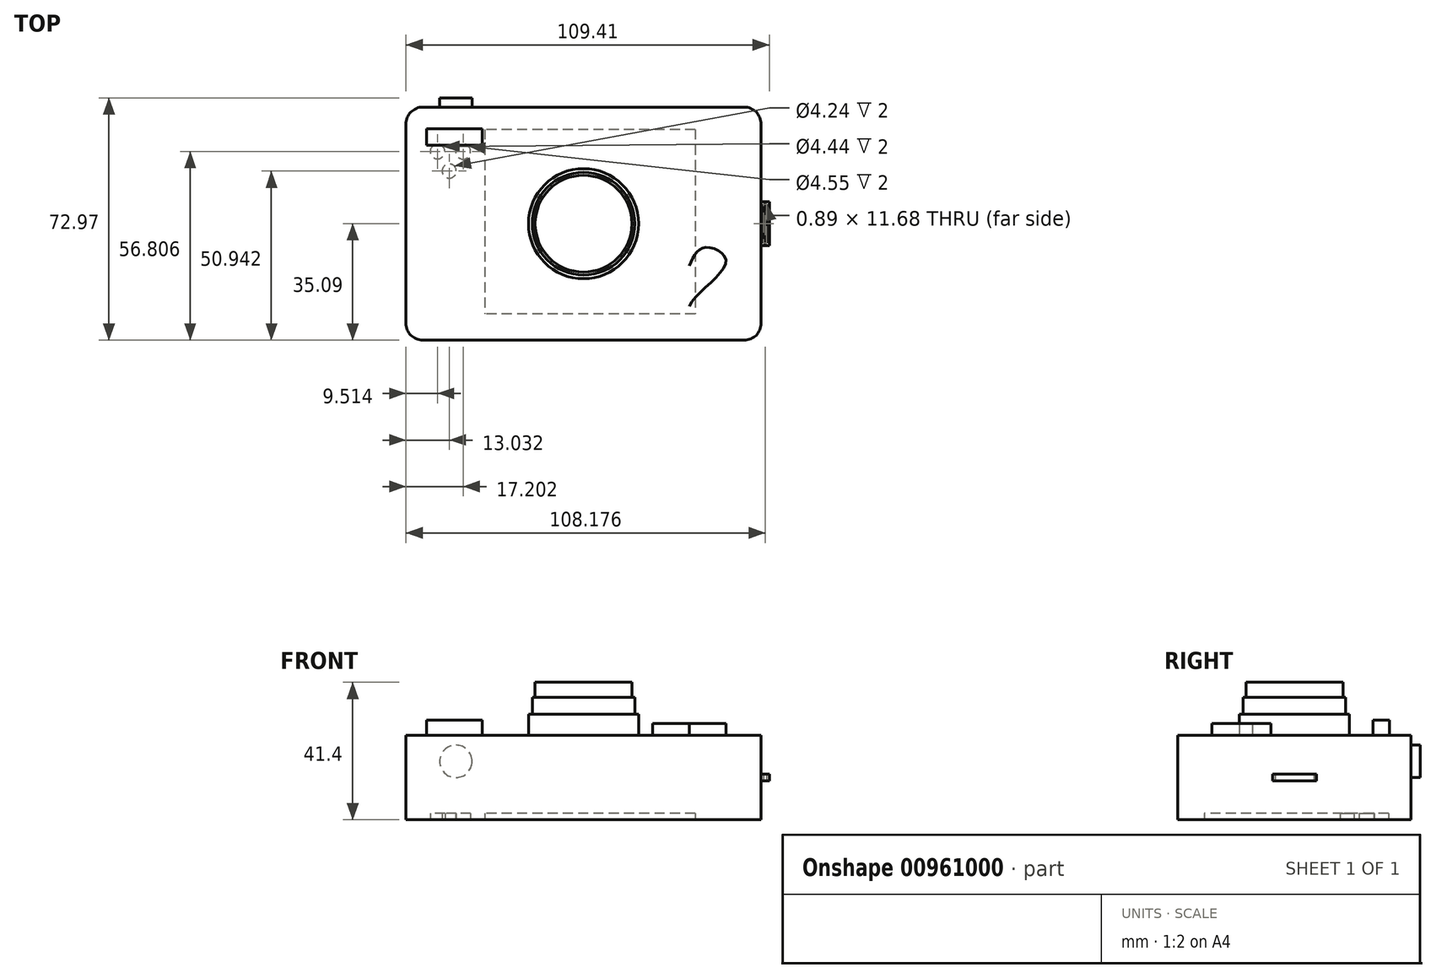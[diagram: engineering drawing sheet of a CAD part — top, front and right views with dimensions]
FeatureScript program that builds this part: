
annotation { "Feature Type Name" : "Feature", "Feature Type Description" : "" }
export const myFeature = defineFeature(function(context is Context, id is Id, definition is map)
    precondition{}
    {
        {
            var Q0;
            Q0=qCreatedBy(makeId("Top.planeOp"),FACE);
            var sketch = newSketch(context, id + "F0", { "sketchPlane" : qUnion([Q0])});
            skLineSegment(sketch, "E0.bottom", {"start": v(53.47, -35.09) * mm, "end": v(-53.47, -35.09) * mm});
            skLineSegment(sketch, "E0.top", {"start": v(53.47, 35.09) * mm, "end": v(-53.47, 35.09) * mm});
            skLineSegment(sketch, "E0.left", {"start": v(53.47, -35.09) * mm, "end": v(53.47, 35.09) * mm});
            skLineSegment(sketch, "E0.right", {"start": v(-53.47, -35.09) * mm, "end": v(-53.47, 35.09) * mm});
            skPoint(sketch, "E0.middle", {"position": v(0, 0) * mm});
            skSolve(sketch);
        }
        {
            var Q0;
            Q0 = qSketchRegion(id + "F0", true);
            extrude(context, id + "F1", {"entities" : qUnion([Q0]), "depth" : 25.4 * mm, "offsetDistance" : 25.4 * mm});
        }
        {
            var Q0;
            Q0=makeQuery(id+"F1.opExtrude","CAP_FACE",FACE,{"disambiguationData":[OSD([sQuery(id+"F0.wireOp",EDGE,"E0.bottom"),sQuery(id+"F0.wireOp",EDGE,"E0.top"),sQuery(id+"F0.wireOp",EDGE,"E0.left"),sQuery(id+"F0.wireOp",EDGE,"E0.right")])],"isStart":false});
            var sketch = newSketch(context, id + "F2", { "sketchPlane" : qUnion([Q0])});
            skCircle(sketch, "E1", {"center": v(0, 0) * mm, "radius": 16.56 * mm});
            skSolve(sketch);
        }
        {
            var Q0;
            Q0 = qSketchRegion(id + "F2", true);
            extrude(context, id + "F3", {"entities" : qUnion([Q0]), "operationType" : NewBodyOperationType.ADD, "depth" : 6.35 * mm, "offsetDistance" : 25.4 * mm});
        }
        {
            var Q0;
            Q0=makeQuery(id+"F3.opExtrude","CAP_FACE",FACE,{"disambiguationData":[OSD([sQuery(id+"F2.wireOp",EDGE,"E1")])],"isStart":false});
            var sketch = newSketch(context, id + "F4", { "sketchPlane" : qUnion([Q0])});
            skCircle(sketch, "E2", {"center": v(0, 0) * mm, "radius": 15.45 * mm});
            skCircle(sketch, "E3", {"center": v(0, 0) * mm, "radius": 14.58 * mm});
            skSolve(sketch);
        }
        {
            var Q0;
            Q0 = qSketchRegion(id + "F4", true);
            extrude(context, id + "F5", {"entities" : qUnion([Q0]), "operationType" : NewBodyOperationType.ADD, "depth" : 5.08 * mm, "offsetDistance" : 25.4 * mm});
        }
        {
            var Q0;
            Q0=makeQuery(id+"F1.opExtrude","CAP_FACE",FACE,{"disambiguationData":[OSD([sQuery(id+"F0.wireOp",EDGE,"E0.bottom"),sQuery(id+"F0.wireOp",EDGE,"E0.top"),sQuery(id+"F0.wireOp",EDGE,"E0.left"),sQuery(id+"F0.wireOp",EDGE,"E0.right")])],"isStart":false});
            var sketch = newSketch(context, id + "F6", { "sketchPlane" : qUnion([Q0])});
            skLineSegment(sketch, "E4.bottom", {"start": v(-30.5, 23.63) * mm, "end": v(-47.29, 23.63) * mm});
            skLineSegment(sketch, "E4.top", {"start": v(-30.5, 28.62) * mm, "end": v(-47.29, 28.62) * mm});
            skLineSegment(sketch, "E4.left", {"start": v(-30.5, 23.63) * mm, "end": v(-30.5, 28.62) * mm});
            skLineSegment(sketch, "E4.right", {"start": v(-47.29, 23.63) * mm, "end": v(-47.29, 28.62) * mm});
            skPoint(sketch, "E4.middle", {"position": v(-38.9, 26.13) * mm});
            skSolve(sketch);
        }
        {
            var Q0;
            Q0 = qSketchRegion(id + "F6", true);
            extrude(context, id + "F7", {"entities" : qUnion([Q0]), "operationType" : NewBodyOperationType.ADD, "depth" : 4.57 * mm, "offsetDistance" : 25.4 * mm});
        }
        {
            var Q0;
            Q0=makeQuery(id+"F1.opExtrude","CAP_FACE",FACE,{"disambiguationData":[OSD([sQuery(id+"F0.wireOp",EDGE,"E0.bottom"),sQuery(id+"F0.wireOp",EDGE,"E0.top"),sQuery(id+"F0.wireOp",EDGE,"E0.left"),sQuery(id+"F0.wireOp",EDGE,"E0.right")])],"isStart":false});
            var sketch = newSketch(context, id + "F8", { "sketchPlane" : qUnion([Q0])});
            skFitSpline(sketch, "E5", {"points": [v(31.84, -12.64) * mm, v(36.6, -7.17) * mm, v(42.85, -11.85) * mm, v(31.84, -26.86) * mm, v(73.26, -31.13) * mm, v(73.72, -30.56) * mm], "startDerivative": vector(21.2, 48.98) * mm, "endDerivative": vector(-1.46, 11.65) * mm});
            skFitSpline(sketch, "E6.MirrorCS", {"points": [v(31.84, -12.64) * mm, v(27.08, -7.17) * mm, v(20.84, -11.85) * mm, v(31.84, -26.86) * mm, v(-9.57, -31.13) * mm, v(-10.04, -30.56) * mm], "startDerivative": vector(-21.2, 48.98) * mm, "endDerivative": vector(1.46, 11.65) * mm});
            skSolve(sketch);
        }
        {
            var Q0;
            Q0=makeQuery(id+"F8.imprint","IMPRINT",FACE,{"disambiguationData":[TD([[makeQuery(id+"F8.imprint","IMPRINT",EDGE,{"derivedFrom":sQuery(id+"F8.wireOp",EDGE,"E5")}),-1.0]])]});
            extrude(context, id + "F9", {"entities" : qUnion([Q0]), "operationType" : NewBodyOperationType.ADD, "depth" : 3.56 * mm, "offsetDistance" : 25.4 * mm});
        }
        {
            var Q0;
            Q0=makeQuery(id+"F1.opExtrude","SWEPT_FACE",FACE,{"disambiguationData":[OSD([sQuery(id+"F0.wireOp",EDGE,"E0.top")])]});
            var sketch = newSketch(context, id + "F10", { "sketchPlane" : qUnion([Q0])});
            skCircle(sketch, "E7", {"center": v(38.43, 17.6) * mm, "radius": 4.87 * mm});
            skSolve(sketch);
        }
        {
            var Q0;
            Q0 = qSketchRegion(id + "F10", true);
            extrude(context, id + "F11", {"entities" : qUnion([Q0]), "operationType" : NewBodyOperationType.ADD, "depth" : 2.8 * mm, "offsetDistance" : 25.4 * mm});
        }
        {
            var Q0;
            Q0=makeQuery(id+"F1.opExtrude","SWEPT_EDGE",EDGE,{"disambiguationData":[OSD([sQuery(id+"F0.wireOp",EDGE,"E0.top"),sQuery(id+"F0.wireOp",EDGE,"E0.left")])]});
            var Q1;
            Q1=makeQuery(id+"F1.opExtrude","SWEPT_EDGE",EDGE,{"disambiguationData":[OSD([sQuery(id+"F0.wireOp",EDGE,"E0.bottom"),sQuery(id+"F0.wireOp",EDGE,"E0.left")])]});
            var Q2;
            Q2=makeQuery(id+"F1.opExtrude","SWEPT_EDGE",EDGE,{"disambiguationData":[OSD([sQuery(id+"F0.wireOp",EDGE,"E0.top"),sQuery(id+"F0.wireOp",EDGE,"E0.right")])]});
            var Q3;
            Q3=makeQuery(id+"F1.opExtrude","SWEPT_EDGE",EDGE,{"disambiguationData":[OSD([sQuery(id+"F0.wireOp",EDGE,"E0.bottom"),sQuery(id+"F0.wireOp",EDGE,"E0.right")])]});
            fillet(context, id + "F12", {"entities" : qUnion([Q0, Q1, Q2, Q3]), "radius" : 5.08 * mm, "tangentPropagation" : true, "allowEdgeOverflow" : false});
        }
        {
            var Q0;
            {var subQ0=sQuery(id+"F0.wireOp",EDGE,"E0.left");Q0=makeQuery(id+"F12.opFillet","BLEND_EDGE",EDGE,{"blendedFrom":[makeQuery(id+"F1.opExtrude","SWEPT_EDGE",EDGE,{"disambiguationData":[OSD([sQuery(id+"F0.wireOp",EDGE,"E0.top"),subQ0])]}),makeQuery(id+"F1.opExtrude","SWEPT_FACE",FACE,{"disambiguationData":[OSD([subQ0])]})],"blendedInto":[makeQuery(id+"F1.opExtrude","SWEPT_FACE",FACE,{"disambiguationData":[OSD([subQ0])]})]});}
            cPoint(context, id + "F13", {"entities" : qUnion([Q0]), "parameter" : 0.5});
        }
        {
            var Q0;
            Q0=qCreatedBy(makeId("Top.planeOp"),FACE);
            var Q1;
            Q1 = qCreatedBy(id + "F13" ,VERTEX);
            cPlane(context, id + "F14", {"entities" : qUnion([Q0, Q1]), "cplaneType" : CPlaneType.PLANE_POINT, "offset" : 25.4 * mm, "width" : 152.4 * mm, "height" : 152.4 * mm});
        }
        {
            var Q0;
            Q0=qCreatedBy(id+"F14.planeOp",FACE);
            var sketch = newSketch(context, id + "F15", { "sketchPlane" : qUnion([Q0])});
            skLineSegment(sketch, "E8.bottom", {"start": v(55.94, 6.63) * mm, "end": v(53.47, 6.63) * mm});
            skLineSegment(sketch, "E8.top", {"start": v(55.94, -6.63) * mm, "end": v(53.47, -6.63) * mm});
            skLineSegment(sketch, "E8.left", {"start": v(55.94, 6.63) * mm, "end": v(55.94, -6.63) * mm});
            skPoint(sketch, "E8.middle", {"position": v(53.47, 0) * mm});
            skLineSegment(sketch, "E9", {"start": v(53.47, -6.63) * mm, "end": v(53.47, 6.63) * mm});
            skPoint(sketch, "E8.right.start.orphan", {"position": v(51, 6.63) * mm});
            skPoint(sketch, "E10.orphan", {"position": v(51, -6.63) * mm});
            skLineSegment(sketch, "E11.0", {"start": v(55.15, 5.84) * mm, "end": v(54.26, 5.84) * mm});
            skLineSegment(sketch, "E11.1", {"start": v(55.15, 5.84) * mm, "end": v(55.15, -5.84) * mm});
            skLineSegment(sketch, "E11.2", {"start": v(55.15, -5.84) * mm, "end": v(54.26, -5.84) * mm});
            skLineSegment(sketch, "E11.3", {"start": v(54.26, -5.84) * mm, "end": v(54.26, 5.84) * mm});
            skSolve(sketch);
        }
        {
            var Q0;
            Q0=makeQuery(id+"F15.imprint","IMPRINT",FACE,{"disambiguationData":[TD([[makeQuery(id+"F15.imprint","IMPRINT",EDGE,{"derivedFrom":sQuery(id+"F15.wireOp",EDGE,"E8.bottom")}),1.0]])]});
            extrude(context, id + "F16", {"entities" : qUnion([Q0]), "operationType" : NewBodyOperationType.ADD, "endBound" : BoundingType.SYMMETRIC, "depth" : 2.03 * mm, "offsetDistance" : 25.4 * mm});
        }
        {
            var Q0;
            Q0=qCreatedBy(makeId("Top.planeOp"),FACE);
            var sketch = newSketch(context, id + "F17", { "sketchPlane" : qUnion([Q0])});
            skLineSegment(sketch, "E12.bottom", {"start": v(33.6, 28.33) * mm, "end": v(-29.69, 28.33) * mm});
            skLineSegment(sketch, "E12.top", {"start": v(33.6, -27.17) * mm, "end": v(-29.69, -27.17) * mm});
            skLineSegment(sketch, "E12.left", {"start": v(33.6, 28.33) * mm, "end": v(33.6, -27.17) * mm});
            skLineSegment(sketch, "E12.right", {"start": v(-29.69, 28.33) * mm, "end": v(-29.69, -27.17) * mm});
            skCircle(sketch, "E13", {"center": v(-40.44, 15.85) * mm, "radius": 2.12 * mm});
            skCircle(sketch, "E14", {"center": v(-43.96, 21.72) * mm, "radius": 2.22 * mm});
            skCircle(sketch, "E15", {"center": v(-36.27, 21.72) * mm, "radius": 2.28 * mm});
            skSolve(sketch);
        }
        {
            var Q0;
            Q0=makeQuery(id+"F17.imprint","IMPRINT",FACE,{"disambiguationData":[TD([[makeQuery(id+"F17.imprint","IMPRINT",EDGE,{"derivedFrom":sQuery(id+"F17.wireOp",EDGE,"E12.bottom")}),1.0]])]});
            var Q1;
            Q1=makeQuery(id+"F17.imprint","IMPRINT",FACE,{"disambiguationData":[TD([[makeQuery(id+"F17.imprint","IMPRINT",EDGE,{"derivedFrom":sQuery(id+"F17.wireOp",EDGE,"E13")}),1.0]])]});
            var Q2;
            Q2=makeQuery(id+"F17.imprint","IMPRINT",FACE,{"disambiguationData":[TD([[makeQuery(id+"F17.imprint","IMPRINT",EDGE,{"derivedFrom":sQuery(id+"F17.wireOp",EDGE,"E14")}),1.0]])]});
            var Q3;
            Q3=makeQuery(id+"F17.imprint","IMPRINT",FACE,{"disambiguationData":[TD([[makeQuery(id+"F17.imprint","IMPRINT",EDGE,{"derivedFrom":sQuery(id+"F17.wireOp",EDGE,"E15")}),1.0]])]});
            extrude(context, id + "F18", {"entities" : qUnion([Q0, Q1, Q2, Q3]), "operationType" : NewBodyOperationType.REMOVE, "depth" : 2 * mm, "offsetDistance" : 25.4 * mm});
        }
        {
            var Q0;
            Q0=makeQuery(id+"F5.boolean.opBoolean","SPLIT",FACE,{"disambiguationData":[TD([makeQuery(id+"F5.opExtrude","SWEPT_FACE",FACE,{"disambiguationData":[OSD([sQuery(id+"F4.wireOp",EDGE,"E3")])]})])],"derivedFrom":makeQuery(id+"F3.opExtrude","CAP_FACE",FACE,{"disambiguationData":[OSD([sQuery(id+"F2.wireOp",EDGE,"E1")])],"isStart":false})});
            extrude(context, id + "F19", {"entities" : qUnion([Q0]), "operationType" : NewBodyOperationType.ADD, "depth" : 9.65 * mm, "offsetDistance" : 25.4 * mm});
        }
    });
